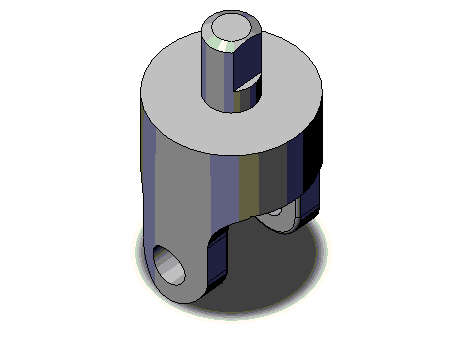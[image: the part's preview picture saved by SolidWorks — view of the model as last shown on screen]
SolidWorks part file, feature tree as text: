
SOLIDWORKS PART (.sldprt)
format: sldprt  version: not decoded by parser v0  size: 292,352 bytes
history: native  units: mm
features: sketch x6, cut_extrude x4, extrude x2, material x1, fillet x1, chamfer x1 (+14 scaffold rows collapsed)
feature tree (29):
  scaffold x14  (default folders/planes/origin — collapsed)
  material  "Material <sin especificar>"
  sketch  "Sketch1"  dims[D1=38.1mm]
  extrude  "Base-Extrude"  Depth=47.625mm
  sketch  "Sketch2"  dims[c1.D3=9.525mm c1.D1=38.1mm c1.D2=19.05mm c2.D3=~29.574791mm c2.D4=29.21mm]
  cut_extrude  "Cut-Extrude1"  [1 undecoded]
  sketch  "Sketch8"  dims[c1.D1=~36.600526mm c1.D2=~36.600526mm c2.D1=10.16mm c2.D2=20.32mm]
  cut_extrude  "Cut-Extrude5"  Depth=47.625mm
  fillet  "Fillet1"  Radius=0.8001mm
  sketch  "Sketch11"  dims[D1=9.525mm D2=~9.574271mm]
  cut_extrude  "Cut-Extrude6"  [1 undecoded]
  sketch  "Sketch12"  dims[D1=12.7mm]
  extrude  "Boss-Extrude1"  Depth=19.05mm
  chamfer  "Chamfer3"  Distance=1.27mm Angle=60deg
  sketch  "Sketch13"  dims[D1=1.5875mm]
  cut_extrude  "Cut-Extrude7"  Depth=12.7mm
decode coverage: 12 of 14 modeling features carry decoded parameters
note: ~ marks probable driven/reference dimensions
note: 2 parameter values undecoded
note: suppression state not decoded; provenance and decode notes live in map.json
